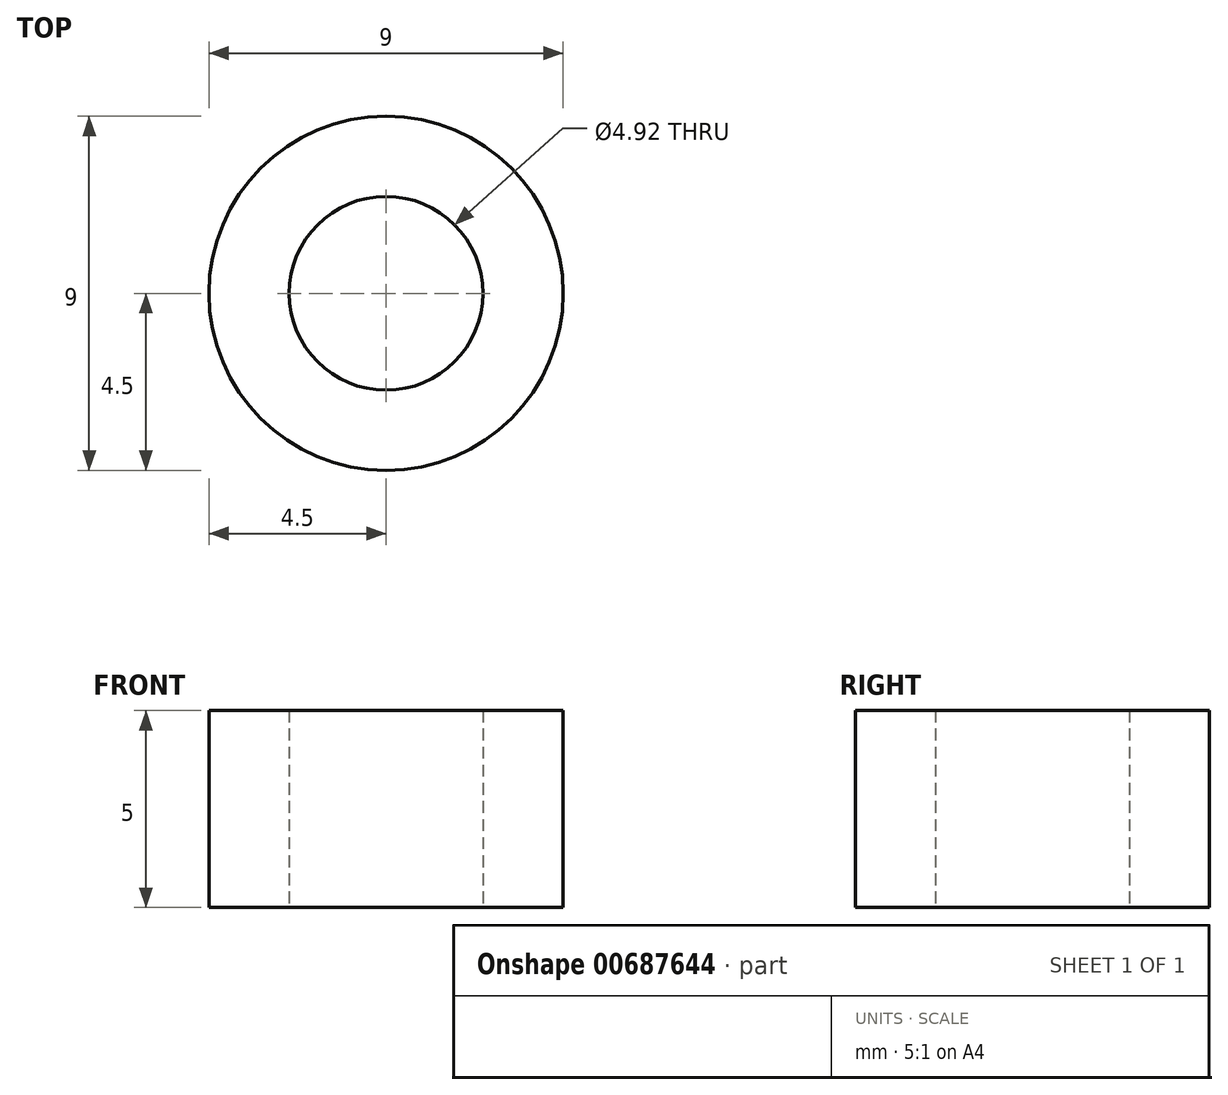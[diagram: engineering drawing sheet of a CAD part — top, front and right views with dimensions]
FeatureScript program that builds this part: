
annotation { "Feature Type Name" : "Feature", "Feature Type Description" : "" }
export const myFeature = defineFeature(function(context is Context, id is Id, definition is map)
    precondition{}
    {
        {
            var Q0;
            Q0=qCreatedBy(makeId("Top.planeOp"),FACE);
            var sketch = newSketch(context, id + "F0", { "sketchPlane" : qUnion([Q0])});
            skCircle(sketch, "E0", {"center": v(0, 0) * mm, "radius": 4.5 * mm});
            skCircle(sketch, "E1", {"center": v(0, 0) * mm, "radius": 2.46 * mm});
            skSolve(sketch);
        }
        {
            var Q0;
            Q0=makeQuery(id+"F0.imprint","IMPRINT",FACE,{"disambiguationData":[TD([[makeQuery(id+"F0.imprint","IMPRINT",EDGE,{"derivedFrom":sQuery(id+"F0.wireOp",EDGE,"E0")}),1.0]])]});
            extrude(context, id + "F1", {"entities" : qUnion([Q0]), "depth" : 5 * mm, "offsetDistance" : 25 * mm});
        }
    });
